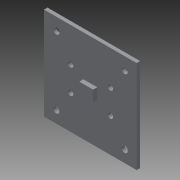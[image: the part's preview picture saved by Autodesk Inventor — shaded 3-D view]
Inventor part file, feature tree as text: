
AUTODESK INVENTOR PART (.ipt)
format: ipt  version: 2014 (Build 180170000, 170)  size: 114,688 bytes
history: native  units: in
note: dims shown in document units (in); Inventor stores cm internally (conversion verified against a paired STEP export)
features: extrude x3, sketch x3
ambient origin geometry x8: Origin, YZ Plane, XZ Plane, XY Plane, X Axis, Y Axis, Z Axis, Center Point
bodies: Solid1 (feature_tree)
feature tree (6):
  extrude  "Extrusion1"  Depth=1.657in
  extrude  "Extrusion2"  Depth=0.062in
  extrude  "Extrusion3"  Depth=0.074in
  sketch  "Sketch1"  dims[d0=1.657in d1=1.657in]
  sketch  "Sketch2"  dims[d2=0.062in d3=0.0in d4=0.1181in]
  sketch  "Sketch3"  dims[d5=0.102in d6=1.105in d7=0.1579in d8=0.1579in d9=1.105in d10=0.1579in d11=0.609in d12=0.335in d13=0.422in d14=0.422in d15=0.559in d16=0.559in d17=0.062in d18=0.0in d19=0.248in d20=0.203in d21=0.727in d22=0.727in d23=0.7045in d24=0.7045in d25=0.074in d26=0.0in]
